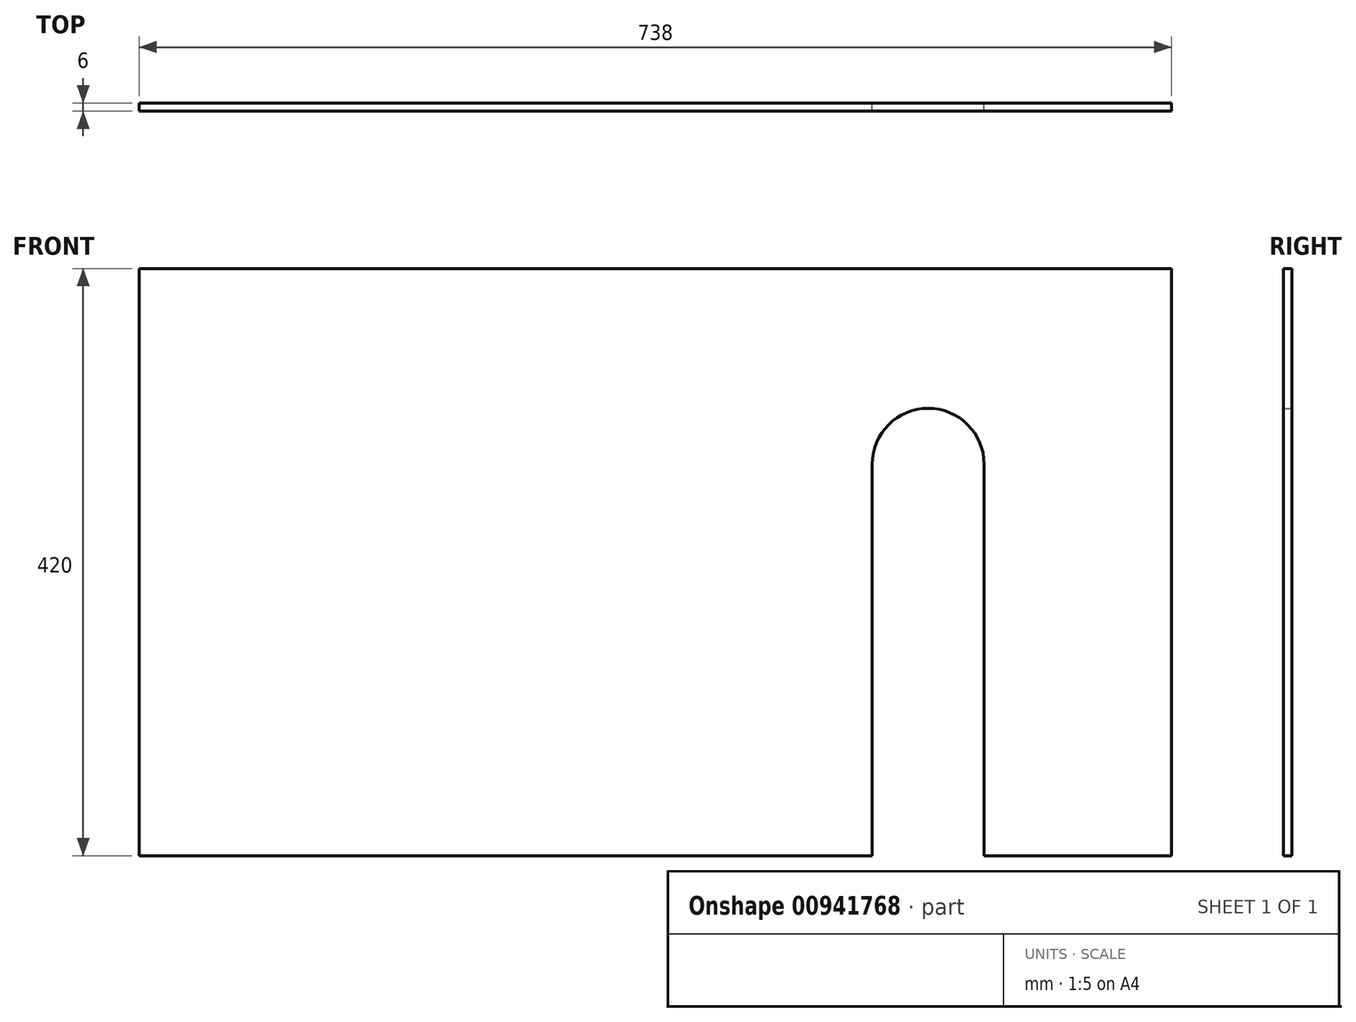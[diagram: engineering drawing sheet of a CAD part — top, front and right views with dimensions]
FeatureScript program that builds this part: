
annotation { "Feature Type Name" : "Feature", "Feature Type Description" : "" }
export const myFeature = defineFeature(function(context is Context, id is Id, definition is map)
    precondition{}
    {
        {
            var Q0;
            Q0=qCreatedBy(makeId("Front.planeOp"),FACE);
            var sketch = newSketch(context, id + "F0", { "sketchPlane" : qUnion([Q0])});
            skLineSegment(sketch, "E0.left", {"start": v(0, 0) * mm, "end": v(0, 420) * mm});
            skLineSegment(sketch, "E0.right", {"start": v(738, 0) * mm, "end": v(738, 420) * mm});
            skLineSegment(sketch, "E1", {"start": v(738, 0) * mm, "end": v(604, 0) * mm});
            skLineSegment(sketch, "E2", {"start": v(0, 0) * mm, "end": v(524, 0) * mm});
            skLineSegment(sketch, "E3", {"start": v(524, 0) * mm, "end": v(524, 280) * mm});
            skLineSegment(sketch, "E4", {"start": v(604, 0) * mm, "end": v(604, 280) * mm});
            skArc(sketch, "E5", {"start": v(604, 280) * mm, "mid": v(564, 320) * mm, "end": v(524, 280) * mm});
            skLineSegment(sketch, "E6", {"start": v(738, 420) * mm, "end": v(0, 420) * mm});
            skSolve(sketch);
        }
        {
            var Q0;
            Q0 = qSketchRegion(id + "F0", true);
            extrude(context, id + "F1", {"entities" : qUnion([Q0]), "depth" : 6 * mm, "offsetDistance" : 25 * mm});
        }
    });
